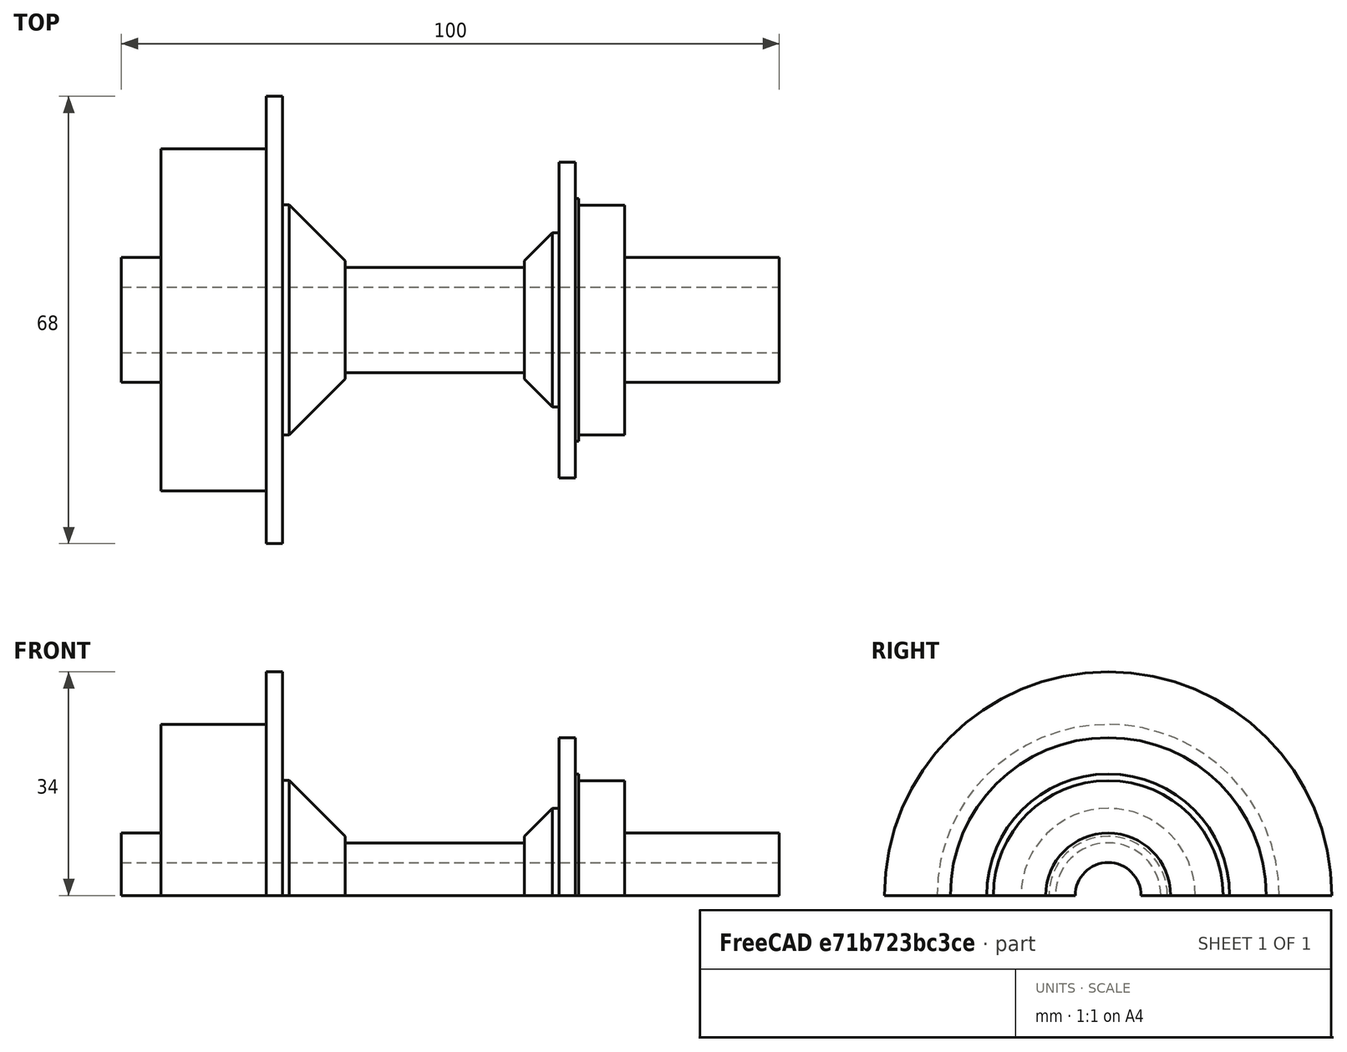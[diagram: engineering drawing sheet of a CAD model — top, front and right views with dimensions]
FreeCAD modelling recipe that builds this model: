
FCSTD DOCUMENT  (FreeCAD 0.16R)
Label: 100mmMTB_wChainline54mmtire
License: All rights reserved
LicenseURL: http://en.wikipedia.org/wiki/All_rights_reserved
objects: Sketcher::SketchObject×1, PartDesign::Revolution×1
note: 3 computed .brp shape members not serialized (recipe doc carries the construction recipe); baked Part::Feature solids carry a one-line shape summary decoded from their .brp

FEATURE [Sketcher::SketchObject] Sketch
  sketch-geometry (57):
    g0: LineSegment StartX=26.5 StartY=9.5 StartZ=0 EndX=26.5 EndY=17.46 EndZ=0
    g1: LineSegment StartX=26.5 StartY=17.46 StartZ=0 EndX=19.5 EndY=17.46 EndZ=0
    g2: LineSegment StartX=19.5 StartY=18.46 StartZ=0 EndX=19 EndY=18.46 EndZ=0
    g3: LineSegment StartX=19 StartY=18.46 StartZ=0 EndX=19 EndY=24 EndZ=0
    g4: LineSegment StartX=19 StartY=24 StartZ=0 EndX=16.5 EndY=24 EndZ=0
    g5: LineSegment StartX=16.5 StartY=24 StartZ=0 EndX=16.5 EndY=13.2426 EndZ=0
    g6: LineSegment StartX=16.5 StartY=13.2426 StartZ=0 EndX=15.5 EndY=13.2426 EndZ=0
    g7: LineSegment StartX=15.5 StartY=13.2426 StartZ=0 EndX=11.2574 EndY=9 EndZ=0
    g8: LineSegment StartX=11.2574 StartY=8 StartZ=0 EndX=-16.0147 EndY=8 EndZ=0
    g9: LineSegment StartX=-25.5 StartY=17.4853 StartZ=0 EndX=-25.5 EndY=34 EndZ=0
    g10: LineSegment StartX=-25.5 StartY=34 StartZ=0 EndX=-28 EndY=34 EndZ=0
    g11: LineSegment StartX=-28 StartY=34 StartZ=0 EndX=-28 EndY=26 EndZ=0
    g12: LineSegment StartX=-44 StartY=26 StartZ=0 EndX=-44 EndY=9.5 EndZ=0
    g13: LineSegment StartX=-24.5 StartY=17.4853 StartZ=0 EndX=-16.0147 EndY=9 EndZ=0
    g14: LineSegment StartX=-25.5 StartY=17.4853 StartZ=0 EndX=-24.5 EndY=17.4853 EndZ=0
    g15: LineSegment StartX=-16.0147 StartY=9 StartZ=0 EndX=-16.0147 EndY=8 EndZ=0
    g16: LineSegment StartX=11.2574 StartY=9 StartZ=0 EndX=11.2574 EndY=8 EndZ=0
    g17: LineSegment StartX=19.5 StartY=18.46 StartZ=0 EndX=19.5 EndY=17.46 EndZ=0
    g18: LineSegment StartX=-44 StartY=26 StartZ=0 EndX=-28 EndY=26 EndZ=0
    g19: LineSegment [constr] StartX=22 StartY=55 StartZ=0 EndX=22 EndY=0 EndZ=0
    g20: LineSegment [constr] StartX=27.5 StartY=45 StartZ=0 EndX=27.5 EndY=20 EndZ=0
    g21: LineSegment [constr] StartX=33 StartY=33 StartZ=0 EndX=33 EndY=20 EndZ=0
    g22: LineSegment [constr] StartX=38.5 StartY=28 StartZ=0 EndX=38.5 EndY=20 EndZ=0
    g23: LineSegment [constr] StartX=44 StartY=22.5 StartZ=0 EndX=44 EndY=9.5 EndZ=0
    g24: LineSegment StartX=-50 StartY=5 StartZ=0 EndX=-50 EndY=9.5 EndZ=0
    g25: LineSegment [constr] StartX=-45.6 StartY=60 StartZ=0 EndX=-44 EndY=60 EndZ=0
    g26: LineSegment [constr] StartX=-44 StartY=60 StartZ=0 EndX=-44 EndY=20 EndZ=0
    g27: LineSegment [constr] StartX=-44 StartY=20 StartZ=0 EndX=-45.6 EndY=20 EndZ=0
    g28: LineSegment [constr] StartX=-45.6 StartY=20 StartZ=0 EndX=-45.6 EndY=60 EndZ=0
    g29: LineSegment [constr] StartX=0 StartY=0 StartZ=0 EndX=0 EndY=193 EndZ=0
    g30: LineSegment [constr] StartX=-28 StartY=34 StartZ=0 EndX=0 EndY=193 EndZ=0
    g31: LineSegment [constr] StartX=19 StartY=24 StartZ=0 EndX=0 EndY=193 EndZ=0
    g32: LineSegment StartX=26.5 StartY=9.5 StartZ=0 EndX=50 EndY=9.5 EndZ=0
    g33: LineSegment StartX=50 StartY=9.5 StartZ=0 EndX=50 EndY=5 EndZ=0
    g34: LineSegment StartX=-50 StartY=5 StartZ=0 EndX=50 EndY=5 EndZ=0
    g35: LineSegment StartX=-44 StartY=9.5 StartZ=0 EndX=-50 EndY=9.5 EndZ=0
    g36: Circle [constr] CenterX=0 CenterY=229 CenterZ=0 NormalX=0 NormalY=0 NormalZ=1 Radius=27
    g37: LineSegment [constr] StartX=-30 StartY=296 StartZ=0 EndX=30 EndY=296 EndZ=0
    g38: LineSegment [constr] StartX=30 StartY=264 StartZ=0 EndX=-30 EndY=264 EndZ=0
    g39: LineSegment [constr] StartX=-30 StartY=264 StartZ=0 EndX=-30 EndY=296 EndZ=0
    g40: LineSegment [constr] StartX=36 StartY=344 StartZ=0 EndX=33 EndY=344 EndZ=0
    g41: LineSegment [constr] StartX=33 StartY=344 StartZ=0 EndX=33 EndY=216 EndZ=0
    g42: LineSegment [constr] StartX=33 StartY=216 StartZ=0 EndX=36 EndY=216 EndZ=0
    g43: LineSegment [constr] StartX=30 StartY=296 StartZ=0 EndX=30 EndY=280 EndZ=0
    g44: LineSegment [constr] StartX=30 StartY=280 StartZ=0 EndX=30 EndY=264 EndZ=0
    g45: LineSegment [constr] StartX=36 StartY=344 StartZ=0 EndX=36 EndY=280 EndZ=0
    g46: LineSegment [constr] StartX=36 StartY=280 StartZ=0 EndX=36 EndY=216 EndZ=0
    g47: LineSegment [constr] StartX=30 StartY=280 StartZ=0 EndX=110 EndY=280 EndZ=0
    g48: LineSegment [constr] StartX=-44 StartY=60 StartZ=0 EndX=-44 EndY=42 EndZ=0
    g49: LineSegment [constr] StartX=-44 StartY=60 StartZ=0 EndX=-28 EndY=60 EndZ=0
    g50: LineSegment [constr] StartX=-28 StartY=60 StartZ=0 EndX=-28 EndY=42 EndZ=0
    g51: LineSegment [constr] StartX=-28 StartY=42 StartZ=0 EndX=-44 EndY=42 EndZ=0
    g52: LineSegment [constr] StartX=-25 StartY=256 StartZ=0 EndX=25 EndY=256 EndZ=0
    g53: LineSegment [constr] StartX=22 StartY=0 StartZ=0 EndX=36 EndY=280 EndZ=0
    g54: LineSegment [constr] StartX=30.8003 StartY=246.093 StartZ=0 EndX=29.1601 EndY=213.288 EndZ=0
    g55: LineSegment [constr] StartX=37.7913 StartY=245.739 StartZ=0 EndX=36.2059 EndY=214.03 EndZ=0
    g56: LineSegment [constr] StartX=36 StartY=280 StartZ=0 EndX=36 EndY=-60.2245 EndZ=0
  constraints (172):
    c: Coincident(g2,g3)
    c: Vertical(g3)
    c: Coincident(g3,g4)
    c: Horizontal(g4)
    c: Coincident(g4,g5)
    c: Vertical(g5)
    c: Coincident(g5,g6)
    c: Coincident(g6,g7)
    c: Horizontal(g8)
    c: Vertical(g9)
    c: Coincident(g9,g10)
    c: Horizontal(g6)
    c: Horizontal(g1)
    c: Horizontal(g10)
    c: DistanceY(g-1,g0) = 9.5
    c: Vertical(g0)
    c: DistanceX(g2,g2) = 0.5
    c: Horizontal(g2)
    c: DistanceY(g-1,g1) = 17.46
    c: DistanceX(g4,g4) = 2.5
    c: DistanceX(g1,g1) = 7
    c: DistanceY(g1,g2) = 1
    c: DistanceY(g-1,g8) = 8
    c: DistanceX(g10,g10) = 2.5
    c: DistanceY(g-1,g4) = 24
    c: Distance(g6) = 1
    c: Angle(g7) = -2.35619
    c: Distance(g7) = 6
    c: Coincident(g10,g11)
    c: Vertical(g12)
    c: Vertical(g11)
    c: DistanceY(g10) = 34
    c: DistanceY(g12) = 26
    c: DistanceX(g12,g11) = 16
    c: Angle(g13) = -0.785398
    c: Distance(g13) = 12
    c: Horizontal(g14)
    c: DistanceX(g14,g14) = 1
    c: Vertical(g15)
    c: Distance(g15) = 1
    c: Coincident(g15,g13)
    c: Coincident(g14,g13)
    c: Coincident(g14,g9)
    c: Coincident(g15,g8)
    c: Vertical(g16)
    c: Distance(g16) = 1
    c: Coincident(g16,g8)
    c: Coincident(g16,g7)
    c: Vertical(g17)
    c: Coincident(g17,g2)
    c: Coincident(g17,g1)
    c: Horizontal(g18)
    c: Coincident(g18,g12)
    c: Coincident(g18,g11)
    c: Vertical(g19)
    c: Vertical(g20)
    c: Vertical(g21)
    c: Vertical(g23)
    c: Vertical(g22)
    c: DistanceX(g19,g20) = 5.5
    c: DistanceX(g20,g21) = 5.5
    c: DistanceX(g21,g22) = 5.5
    c: DistanceX(g22,g23) = 5.5
    c: DistanceY(g19) = 55
    c: DistanceX(g2,g19) = 3
    c: Vertical(g24)
    c: Coincident(g25,g26)
    c: Coincident(g26,g27)
    c: Coincident(g27,g28)
    c: Coincident(g28,g25)
    c: Horizontal(g25)
    c: Horizontal(g27)
    c: Vertical(g26)
    c: Vertical(g28)
    c: DistanceX(g25,g25) = 1.6
    c: PointOnObject(g29,g-1)
    c: Vertical(g29)
    c: Distance(g29) = 193
    c: Coincident(g30,g29)
    c: Coincident(g30,g31)
    c: Coincident(g31,g3)
    c: Coincident(g30,g10)
    c: DistanceY(g22) = 20
    c: DistanceY(g21) = 20
    c: DistanceY(g20) = 20
    c: Distance(g20) = 25
    c: Distance(g22) = 8
    c: Distance(g21) = 13
    c: DistanceY(g23,g23) = 13
    c: Coincident(g1,g0)
    c: Coincident(g34,g33)
    c: Horizontal(g34)
    c: Vertical(g33)
    c: Distance(g32,g23) = 6
    c: Coincident(g33,g32)
    c: PointOnObject(g23,g32)
    c: Horizontal(g32)
    c: DistanceY(g32) = 9.5
    c: DistanceY(g33) = 5
    c: DistanceX(g24,g33) = 100
    c: DistanceX(g24,g29) = 50
    c: Coincident(g35,g12)
    c: Coincident(g35,g24)
    c: DistanceY(g26) = 20
    c: Coincident(g24,g34)
    c: Horizontal(g35)
    c: DistanceY(g12) = 9.5
    c: PointOnObject(g26,g12)
    c: DistanceX(g35,g35) = 6
    c: Coincident(g32,g0)
    c: Coincident(g-1,g29)
    c: Radius(g36) = 27
    c: PointOnObject(g36,g-2)
    c: Coincident(g38,g39)
    c: Coincident(g39,g37)
    c: Horizontal(g37)
    c: Horizontal(g38)
    c: Vertical(g39)
    c: Symmetric(g38,g38,g-2)
    c: Distance(g37) = 60
    c: Coincident(g40,g41)
    c: Coincident(g41,g42)
    c: Horizontal(g40)
    c: Horizontal(g42)
    c: Vertical(g41)
    c: Distance(g42) = 3
    c: Distance(g41) = 128
    c: Vertical(g43)
    c: Coincident(g44,g43)
    c: Coincident(g43,g37)
    c: Coincident(g44,g38)
    c: Symmetric(g37,g38,g43)
    c: Vertical(g45)
    c: Coincident(g46,g42)
    c: Coincident(g45,g40)
    c: Vertical(g46)
    c: Coincident(g46,g45)
    c: Horizontal(g47)
    c: Coincident(g47,g43)
    c: Distance(g47) = 80
    c: PointOnObject(g45,g47)
    c: DistanceX(g43,g45) = 6
    c: Vertical(g48)
    c: Horizontal(g49)
    c: Coincident(g49,g50)
    c: Coincident(g50,g51)
    c: Coincident(g51,g48)
    c: Horizontal(g51)
    c: Vertical(g50)
    c: Distance(g51) = 16
    c: Coincident(g49,g48)
    c: Distance(g50) = 18
    c: PointOnObject(g48,g26)
    c: Coincident(g48,g25)
    c: DistanceY(g25) = 60
    c: DistanceY(g43) = 280
    c: Distance(g39) = 32
    c: Symmetric(g42,g40,g47)
    c: Tangent(g52,g36)
    c: Horizontal(g52)
    c: Symmetric(g52,g52,g-2)
    c: DistanceY(g-1,g52) = 256
    c: PointOnObject(g19,g-1)
    c: Coincident(g53,g19)
    c: Coincident(g53,g45)
    c: Distance(g52) = 50
    c: Parallel(g54,g53)
    c: Parallel(g55,g53)
    c: Distance(g54,g53) = 3.5
    c: Distance(g55,g53) = 3.5
    c: Coincident(g56,g45)
    c: Vertical(g56)
FEATURE [PartDesign::Revolution] Revolution
  Angle = 180
  Axis = (1,0,0)
  Base = (0,0,0)
  ReferenceAxis = -> Sketch [H_Axis]
  Sketch = -> Sketch
